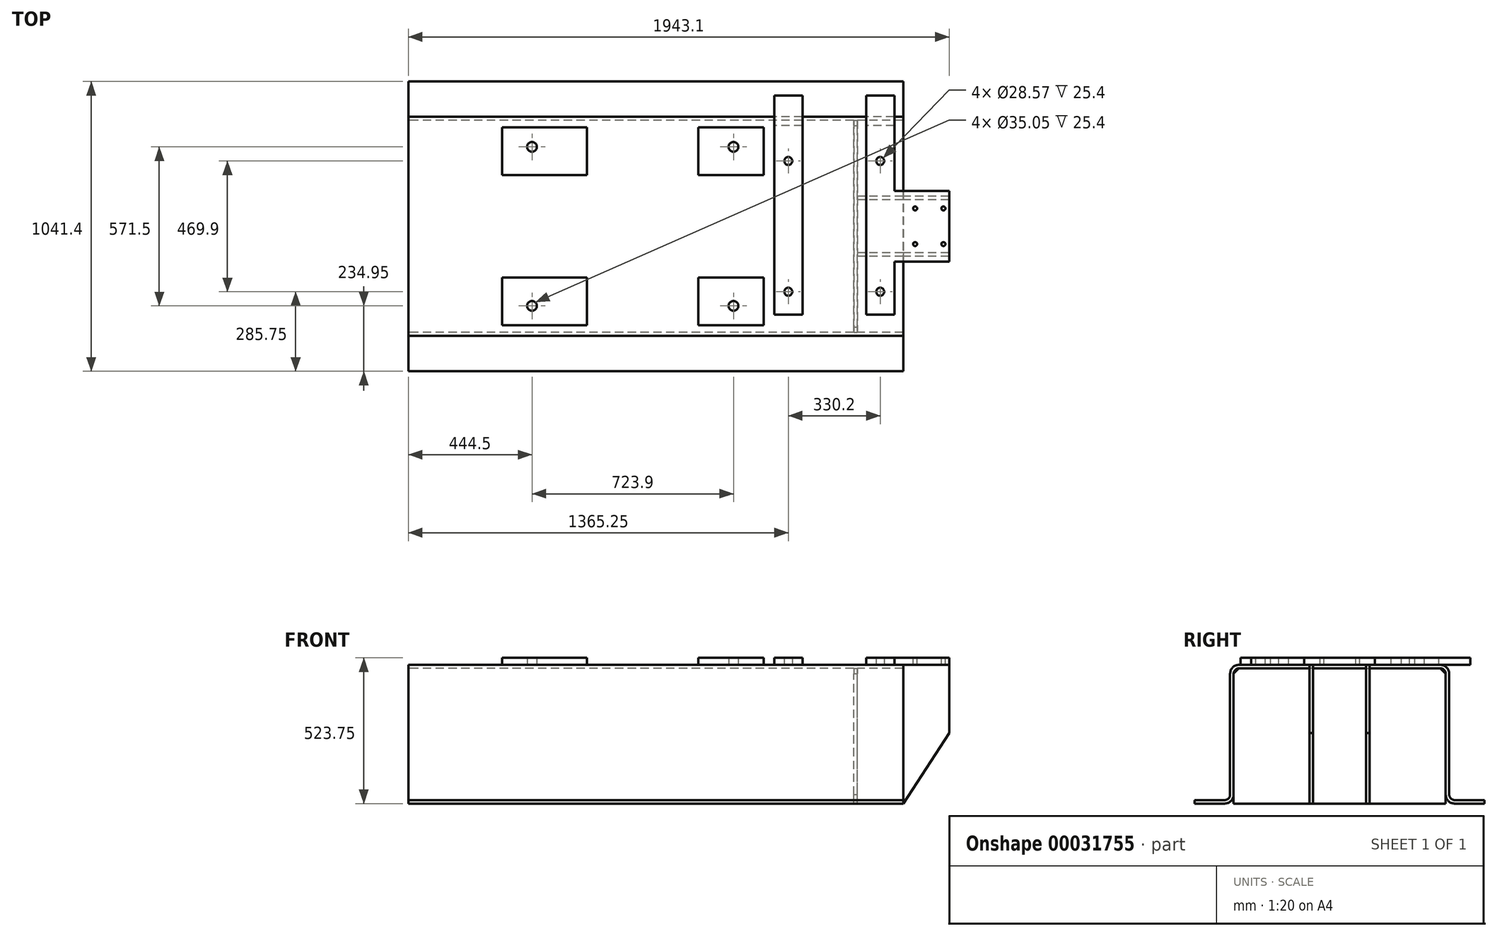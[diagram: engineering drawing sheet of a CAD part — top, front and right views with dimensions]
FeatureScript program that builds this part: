
annotation { "Feature Type Name" : "Feature", "Feature Type Description" : "" }
export const myFeature = defineFeature(function(context is Context, id is Id, definition is map)
    precondition{}
    {
        {
            var Q0;
            Q0=qCreatedBy(makeId("Right.planeOp"),FACE);
            var sketch = newSketch(context, id + "F0", { "sketchPlane" : qUnion([Q0])});
            skLineSegment(sketch, "E0", {"start": v(-520.7, 0) * mm, "end": v(-412.75, 0) * mm});
            skLineSegment(sketch, "E1.0", {"start": v(-520.7, 12.7) * mm, "end": v(-412.75, 12.7) * mm});
            skLineSegment(sketch, "E2", {"start": v(-520.7, 0) * mm, "end": v(-520.7, 12.7) * mm});
            skLineSegment(sketch, "E3", {"start": v(0, 498.35) * mm, "end": v(0, -237.5) * mm, "construction": true});
            skLineSegment(sketch, "E4.0", {"start": v(-381, 31.75) * mm, "end": v(-381, 466.6) * mm});
            skLineSegment(sketch, "E5.0", {"start": v(-393.7, 31.75) * mm, "end": v(-393.7, 466.6) * mm});
            skLineSegment(sketch, "E6.0", {"start": v(-361.95, 498.35) * mm, "end": v(0, 498.35) * mm});
            skLineSegment(sketch, "E7.0", {"start": v(-361.95, 485.65) * mm, "end": v(0, 485.65) * mm});
            skPoint(sketch, "E8.orphan", {"position": v(-520.7, 181.66) * mm});
            skPoint(sketch, "E9.visualSharp", {"position": v(-381, 485.65) * mm});
            skArc(sketch, "E9.filletArc", {"start": v(-361.95, 485.65) * mm, "mid": v(-375.42, 480.07) * mm, "end": v(-381, 466.6) * mm});
            skPoint(sketch, "E10.visualSharp", {"position": v(-393.7, 12.7) * mm});
            skArc(sketch, "E10.filletArc", {"start": v(-412.75, 12.7) * mm, "mid": v(-399.28, 18.28) * mm, "end": v(-393.7, 31.75) * mm});
            skPoint(sketch, "E11.visualSharp", {"position": v(-393.7, 498.35) * mm});
            skArc(sketch, "E11.filletArc", {"start": v(-361.95, 498.35) * mm, "mid": v(-384.4, 489.05) * mm, "end": v(-393.7, 466.6) * mm});
            skPoint(sketch, "E12.visualSharp", {"position": v(-381, 0) * mm});
            skArc(sketch, "E12.filletArc", {"start": v(-412.75, 0) * mm, "mid": v(-390.3, 9.3) * mm, "end": v(-381, 31.75) * mm});
            skLineSegment(sketch, "E13.MirrorCS", {"start": v(520.7, 0) * mm, "end": v(520.7, 12.7) * mm});
            skArc(sketch, "E14.MirrorCS", {"start": v(412.75, 12.7) * mm, "mid": v(399.28, 18.28) * mm, "end": v(393.7, 31.75) * mm});
            skArc(sketch, "E15.MirrorCS", {"start": v(412.75, 0) * mm, "mid": v(390.3, 9.3) * mm, "end": v(381, 31.75) * mm});
            skPoint(sketch, "E16.MirrorP", {"position": v(393.7, 12.7) * mm});
            skPoint(sketch, "E17.MirrorP", {"position": v(381, 0) * mm});
            skLineSegment(sketch, "E18.MirrorCS", {"start": v(520.7, 0) * mm, "end": v(412.75, 0) * mm});
            skLineSegment(sketch, "E19.MirrorCS", {"start": v(520.7, 12.7) * mm, "end": v(412.75, 12.7) * mm});
            skLineSegment(sketch, "E20.MirrorCS", {"start": v(393.7, 31.75) * mm, "end": v(393.7, 466.6) * mm});
            skLineSegment(sketch, "E21.MirrorCS", {"start": v(381, 31.75) * mm, "end": v(381, 466.6) * mm});
            skArc(sketch, "E22.MirrorCS", {"start": v(361.95, 485.65) * mm, "mid": v(375.42, 480.07) * mm, "end": v(381, 466.6) * mm});
            skArc(sketch, "E23.MirrorCS", {"start": v(361.95, 498.35) * mm, "mid": v(384.4, 489.05) * mm, "end": v(393.7, 466.6) * mm});
            skPoint(sketch, "E24.MirrorP", {"position": v(381, 485.65) * mm});
            skPoint(sketch, "E25.MirrorP", {"position": v(393.7, 498.35) * mm});
            skLineSegment(sketch, "E26.MirrorCS", {"start": v(361.95, 485.65) * mm, "end": v(0, 485.65) * mm});
            skLineSegment(sketch, "E27.MirrorCS", {"start": v(361.95, 498.35) * mm, "end": v(0, 498.35) * mm});
            skSolve(sketch);
        }
        {
            var Q0;
            Q0 = qSketchRegion(id + "F0", true);
            extrude(context, id + "F1", {"entities" : qUnion([Q0]), "endBound" : BoundingType.SYMMETRIC, "depth" : 1778 * mm});
        }
        {
            var Q0;
            Q0=makeQuery(id+"F1.opExtrude","SWEPT_FACE",FACE,{"disambiguationData":[OSD([sQuery(id+"F0.wireOp",EDGE,"E6.0"),sQuery(id+"F0.wireOp",EDGE,"E27.MirrorCS")])]});
            var sketch = newSketch(context, id + "F2", { "sketchPlane" : qUnion([Q0])});
            skLineSegment(sketch, "E28.0", {"start": v(641.35, 361.95) * mm, "end": v(641.35, -361.95) * mm, "construction": true});
            skLineSegment(sketch, "E29.0", {"start": v(-82.55, 361.95) * mm, "end": v(-82.55, -361.95) * mm, "construction": true});
            skLineSegment(sketch, "E30", {"start": v(-872.47, 0) * mm, "end": v(1054.1, 0) * mm, "construction": true});
            skLineSegment(sketch, "E31.0", {"start": v(476.25, 361.95) * mm, "end": v(476.25, -361.95) * mm, "construction": true});
            skLineSegment(sketch, "E32.0", {"start": v(806.45, 361.95) * mm, "end": v(806.45, -361.95) * mm, "construction": true});
            skLineSegment(sketch, "E33.0", {"start": v(425.45, 469.9) * mm, "end": v(425.45, -317.5) * mm});
            skLineSegment(sketch, "E34.0", {"start": v(527.05, 469.9) * mm, "end": v(527.05, -317.5) * mm});
            skLineSegment(sketch, "E35.0", {"start": v(755.65, 469.9) * mm, "end": v(755.65, -317.5) * mm});
            skLineSegment(sketch, "E36.0", {"start": v(1054.1, 127) * mm, "end": v(1054.1, -127) * mm});
            skLineSegment(sketch, "E37.0", {"start": v(425.45, 469.9) * mm, "end": v(527.05, 469.9) * mm});
            skLineSegment(sketch, "E38.0", {"start": v(755.65, -317.5) * mm, "end": v(857.25, -317.5) * mm});
            skLineSegment(sketch, "E39.trimOffspring", {"start": v(755.65, 469.9) * mm, "end": v(857.25, 469.9) * mm});
            skLineSegment(sketch, "E40.trimOffspring", {"start": v(527.05, -317.5) * mm, "end": v(425.45, -317.5) * mm});
            skLineSegment(sketch, "E41.0", {"start": v(857.25, 469.9) * mm, "end": v(857.25, 127) * mm});
            skLineSegment(sketch, "E42.trimOffspring", {"start": v(857.25, -127) * mm, "end": v(1054.1, -127) * mm});
            skLineSegment(sketch, "E43.trimOffspring", {"start": v(857.25, 127) * mm, "end": v(1054.1, 127) * mm});
            skLineSegment(sketch, "E44.trimOffspring", {"start": v(857.25, -127) * mm, "end": v(857.25, -317.5) * mm});
            skLineSegment(sketch, "E45.0", {"start": v(-872.47, 234.95) * mm, "end": v(1054.1, 234.95) * mm, "construction": true});
            skCircle(sketch, "E46", {"center": v(476.25, 234.95) * mm, "radius": 14.29 * mm});
            skCircle(sketch, "E47", {"center": v(806.45, 234.95) * mm, "radius": 14.29 * mm});
            skCircle(sketch, "E48.MirrorC", {"center": v(806.45, -234.95) * mm, "radius": 14.29 * mm});
            skCircle(sketch, "E49.MirrorC", {"center": v(476.25, -234.95) * mm, "radius": 14.29 * mm});
            skSolve(sketch);
        }
        {
            var Q0;
            Q0 = qSketchRegion(id + "F2", true);
            extrude(context, id + "F3", {"entities" : qUnion([Q0]), "operationType" : NewBodyOperationType.ADD, "depth" : 25.4 * mm});
        }
        {
            var Q0;
            Q0=makeQuery(id+"F3.opExtrude","CAP_FACE",FACE,{"disambiguationData":[OSD([sQuery(id+"F2.wireOp",EDGE,"E35.0"),sQuery(id+"F2.wireOp",EDGE,"E36.0"),sQuery(id+"F2.wireOp",EDGE,"E38.0"),sQuery(id+"F2.wireOp",EDGE,"E39.trimOffspring"),sQuery(id+"F2.wireOp",EDGE,"E41.0"),sQuery(id+"F2.wireOp",EDGE,"E42.trimOffspring"),sQuery(id+"F2.wireOp",EDGE,"E43.trimOffspring"),sQuery(id+"F2.wireOp",EDGE,"E44.trimOffspring"),sQuery(id+"F2.wireOp",EDGE,"E47"),sQuery(id+"F2.wireOp",EDGE,"E48.MirrorC")])],"isStart":false});
            var sketch = newSketch(context, id + "F4", { "sketchPlane" : qUnion([Q0])});
            skLineSegment(sketch, "E50", {"start": v(806.45, 234.95) * mm, "end": v(806.45, -249.24) * mm, "construction": true});
            skLineSegment(sketch, "E51", {"start": v(0, 0) * mm, "end": v(1216.03, 0) * mm, "construction": true});
            skPoint(sketch, "E51.endSnap0", {"position": v(1054.1, 0) * mm});
            skLineSegment(sketch, "E52.0", {"start": v(931.93, 234.95) * mm, "end": v(931.93, -249.24) * mm, "construction": true});
            skLineSegment(sketch, "E53.0", {"start": v(1033.53, 234.95) * mm, "end": v(1033.53, -249.24) * mm, "construction": true});
            skLineSegment(sketch, "E54.0", {"start": v(0, 64.52) * mm, "end": v(1216.03, 64.52) * mm, "construction": true});
            skLineSegment(sketch, "E55.0", {"start": v(0, -63.5) * mm, "end": v(1216.03, -63.5) * mm, "construction": true});
            skCircle(sketch, "E56", {"center": v(931.93, 64.52) * mm, "radius": 7.14 * mm});
            skCircle(sketch, "E57", {"center": v(1033.53, 64.52) * mm, "radius": 7.14 * mm});
            skCircle(sketch, "E58", {"center": v(1033.53, -63.5) * mm, "radius": 7.14 * mm});
            skCircle(sketch, "E59", {"center": v(931.93, -63.5) * mm, "radius": 7.14 * mm});
            skSolve(sketch);
        }
        {
            var Q0;
            Q0 = qSketchRegion(id + "F4", true);
            extrude(context, id + "F5", {"entities" : qUnion([Q0]), "operationType" : NewBodyOperationType.REMOVE, "endBound" : BoundingType.THROUGH_ALL, "oppositeDirection" : true, "depth" : 25.4 * mm});
        }
        {
            var Q0;
            Q0=makeQuery(id+"F1.opExtrude","CAP_FACE",FACE,{"disambiguationData":[OSD([sQuery(id+"F0.wireOp",EDGE,"E0"),sQuery(id+"F0.wireOp",EDGE,"E1.0"),sQuery(id+"F0.wireOp",EDGE,"E2"),sQuery(id+"F0.wireOp",EDGE,"E4.0"),sQuery(id+"F0.wireOp",EDGE,"E5.0"),sQuery(id+"F0.wireOp",EDGE,"E6.0"),sQuery(id+"F0.wireOp",EDGE,"E7.0"),sQuery(id+"F0.wireOp",EDGE,"E9.filletArc"),sQuery(id+"F0.wireOp",EDGE,"E10.filletArc"),sQuery(id+"F0.wireOp",EDGE,"E11.filletArc"),sQuery(id+"F0.wireOp",EDGE,"E12.filletArc"),sQuery(id+"F0.wireOp",EDGE,"E13.MirrorCS"),sQuery(id+"F0.wireOp",EDGE,"E14.MirrorCS"),sQuery(id+"F0.wireOp",EDGE,"E15.MirrorCS"),sQuery(id+"F0.wireOp",EDGE,"E18.MirrorCS"),sQuery(id+"F0.wireOp",EDGE,"E19.MirrorCS"),sQuery(id+"F0.wireOp",EDGE,"E22.MirrorCS"),sQuery(id+"F0.wireOp",EDGE,"E23.MirrorCS"),sQuery(id+"F0.wireOp",EDGE,"E26.MirrorCS"),sQuery(id+"F0.wireOp",EDGE,"E27.MirrorCS"),sQuery(id+"F0.wireOp",EDGE,"E20.MirrorCS"),sQuery(id+"F0.wireOp",EDGE,"E21.MirrorCS")])],"isStart":false});
            cPlane(context, id + "F6", {"entities" : qUnion([Q0]), "cplaneType" : CPlaneType.OFFSET, "offset" : 165.1 * mm, "oppositeDirection" : true, "width" : 152.4 * mm, "height" : 152.4 * mm});
        }
        {
            var Q0;
            Q0=qCreatedBy(id+"F6.planeOp",FACE);
            var sketch = newSketch(context, id + "F7", { "sketchPlane" : qUnion([Q0])});
            skLineSegment(sketch, "E60.0", {"start": v(-361.95, 485.65) * mm, "end": v(361.95, 485.65) * mm});
            skLineSegment(sketch, "E61.0", {"start": v(-381, 0) * mm, "end": v(-381, 466.6) * mm});
            skLineSegment(sketch, "E62.0", {"start": v(381, 0) * mm, "end": v(381, 466.6) * mm});
            skLineSegment(sketch, "E63.0", {"start": v(381, 0) * mm, "end": v(-381, 0) * mm});
            skPoint(sketch, "E64.orphan", {"position": v(412.75, 0) * mm});
            skPoint(sketch, "E65.orphan", {"position": v(520.7, 0) * mm});
            skPoint(sketch, "E66.orphan", {"position": v(381, 31.75) * mm});
            skPoint(sketch, "E67.orphan", {"position": v(-381, 31.75) * mm});
            skLineSegment(sketch, "E68", {"start": v(-381, 466.6) * mm, "end": v(-361.95, 485.65) * mm});
            skLineSegment(sketch, "E69", {"start": v(361.95, 485.65) * mm, "end": v(381, 466.6) * mm});
            skSolve(sketch);
        }
        {
            var Q0;
            Q0 = qSketchRegion(id + "F7", true);
            extrude(context, id + "F8", {"entities" : qUnion([Q0]), "operationType" : NewBodyOperationType.ADD, "oppositeDirection" : true, "depth" : 12.7 * mm});
        }
        {
            var Q0;
            Q0=makeQuery(id+"F8.opExtrude","CAP_FACE",FACE,{"disambiguationData":[OSD([sQuery(id+"F7.wireOp",EDGE,"E60.0"),sQuery(id+"F7.wireOp",EDGE,"E61.0"),sQuery(id+"F7.wireOp",EDGE,"E62.0"),sQuery(id+"F7.wireOp",EDGE,"E63.0"),sQuery(id+"F7.wireOp",EDGE,"E68"),sQuery(id+"F7.wireOp",EDGE,"E69")])],"isStart":true});
            var sketch = newSketch(context, id + "F9", { "sketchPlane" : qUnion([Q0])});
            skLineSegment(sketch, "E70", {"start": v(0, 0) * mm, "end": v(0, 673.02) * mm, "construction": true});
            skPoint(sketch, "E70.endSnap0", {"position": v(0, 0) * mm});
            skLineSegment(sketch, "E71.0", {"start": v(-95.25, 0) * mm, "end": v(-95.25, 673.02) * mm, "construction": true});
            skLineSegment(sketch, "E72.bottom", {"start": v(-95.25, 0) * mm, "end": v(-107.95, 0) * mm});
            skLineSegment(sketch, "E72.top", {"start": v(-95.25, 485.65) * mm, "end": v(-107.95, 485.65) * mm});
            skLineSegment(sketch, "E72.left", {"start": v(-95.25, 0) * mm, "end": v(-95.25, 485.65) * mm});
            skLineSegment(sketch, "E72.right", {"start": v(-107.95, 0) * mm, "end": v(-107.95, 485.65) * mm});
            skSolve(sketch);
        }
        {
            var Q0;
            Q0 = qSketchRegion(id + "F9", true);
            var Q1;
            Q1=makeQuery(id+"F3.opExtrude","SWEPT_FACE",FACE,{"disambiguationData":[OSD([sQuery(id+"F2.wireOp",EDGE,"E36.0")])]});
            extrude(context, id + "F10", {"entities" : qUnion([Q0]), "endBound" : BoundingType.UP_TO_SURFACE, "endBoundEntityFace" : qUnion([Q1]), "depth" : 25.4 * mm});
        }
        {
            var Q0;
            Q0=makeQuery(id+"F10.opExtrude","SWEPT_FACE",FACE,{"disambiguationData":[OSD([sQuery(id+"F9.wireOp",EDGE,"E72.right")])]});
            var sketch = newSketch(context, id + "F11", { "sketchPlane" : qUnion([Q0])});
            skPoint(sketch, "E73.oppositeSnap0", {"position": v(889, 485.65) * mm});
            skLineSegment(sketch, "E73.bottom", {"start": v(1054.1, 485.65) * mm, "end": v(889, 485.65) * mm});
            skLineSegment(sketch, "E73.top", {"start": v(1054.1, 498.55) * mm, "end": v(889, 498.55) * mm});
            skLineSegment(sketch, "E73.left", {"start": v(1054.1, 485.65) * mm, "end": v(1054.1, 498.55) * mm});
            skLineSegment(sketch, "E73.right", {"start": v(889, 485.65) * mm, "end": v(889, 498.55) * mm});
            skSolve(sketch);
        }
        {
            var Q0;
            Q0 = qSketchRegion(id + "F11", true);
            extrude(context, id + "F12", {"entities" : qUnion([Q0]), "oppositeDirection" : true, "depth" : 12.7 * mm});
        }
        {
            var Q0;
            Q0=makeQuery(id+"F12.opExtrude","SWEPT_BODY",BODY,{"disambiguationData":[OSD([sQuery(id+"F11.wireOp",EDGE,"E73.bottom"),sQuery(id+"F11.wireOp",EDGE,"E73.top"),sQuery(id+"F11.wireOp",EDGE,"E73.left"),sQuery(id+"F11.wireOp",EDGE,"E73.right")])]});
            var Q1;
            Q1=makeQuery(id+"F10.opExtrude","SWEPT_BODY",BODY,{"disambiguationData":[OSD([sQuery(id+"F9.wireOp",EDGE,"E72.bottom"),sQuery(id+"F9.wireOp",EDGE,"E72.top"),sQuery(id+"F9.wireOp",EDGE,"E72.left"),sQuery(id+"F9.wireOp",EDGE,"E72.right")])]});
            booleanBodies(context, id + "F13", {"operationType" : BooleanOperationType.UNION, "tools" : qUnion([Q0, Q1])});
        }
        {
            var Q0;
            Q0=makeQuery(id+"F13.opBoolean","MERGE",FACE,{"derivedFrom":[makeQuery(id+"F10.opExtrude","SWEPT_FACE",FACE,{"disambiguationData":[OSD([sQuery(id+"F9.wireOp",EDGE,"E72.right")])]}),makeQuery(id+"F12.opExtrude","CAP_FACE",FACE,{"disambiguationData":[OSD([sQuery(id+"F11.wireOp",EDGE,"E73.bottom"),sQuery(id+"F11.wireOp",EDGE,"E73.top"),sQuery(id+"F11.wireOp",EDGE,"E73.left"),sQuery(id+"F11.wireOp",EDGE,"E73.right")])],"isStart":true})]});
            var sketch = newSketch(context, id + "F14", { "sketchPlane" : qUnion([Q0])});
            skLineSegment(sketch, "E74.0", {"start": v(1054.1, 0) * mm, "end": v(723.9, 0) * mm, "construction": true});
            skLineSegment(sketch, "E75.0", {"start": v(889, 0) * mm, "end": v(889, 12.7) * mm, "construction": true});
            skLineSegment(sketch, "E76.0", {"start": v(1054.1, 254) * mm, "end": v(723.9, 254) * mm, "construction": true});
            skLineSegment(sketch, "E77", {"start": v(1054.1, 254) * mm, "end": v(889, 0) * mm});
            skLineSegment(sketch, "E78", {"start": v(889, 0) * mm, "end": v(1054.1, 0) * mm});
            skLineSegment(sketch, "E79", {"start": v(1054.1, 0) * mm, "end": v(1054.1, 254) * mm});
            skSolve(sketch);
        }
        {
            var Q0;
            Q0 = qSketchRegion(id + "F14", true);
            extrude(context, id + "F15", {"entities" : qUnion([Q0]), "operationType" : NewBodyOperationType.REMOVE, "endBound" : BoundingType.THROUGH_ALL, "oppositeDirection" : true, "depth" : 25.4 * mm});
        }
        {
            var Q0;
            Q0=makeQuery(id+"F12.opExtrude","SWEPT_BODY",BODY,{"disambiguationData":[OSD([sQuery(id+"F11.wireOp",EDGE,"E73.bottom"),sQuery(id+"F11.wireOp",EDGE,"E73.top"),sQuery(id+"F11.wireOp",EDGE,"E73.left"),sQuery(id+"F11.wireOp",EDGE,"E73.right")])]});
            var Q1;
            Q1=qCreatedBy(makeId("Front.planeOp"),FACE);
            mirror(context, id + "F16", {"entities" : qUnion([Q0]), "mirrorPlane" : qUnion([Q1])});
        }
        {
            var Q0;
            {var subQ0=sQuery(id+"F0.wireOp",EDGE,"E6.0");var subQ1=sQuery(id+"F0.wireOp",EDGE,"E27.MirrorCS");var subQ9=sQuery(id+"F0.wireOp",EDGE,"E11.filletArc");Q0=makeQuery(id+"F3.boolean.opBoolean","SPLIT",FACE,{"disambiguationData":[TD([makeQuery(id+"F1.opExtrude","SWEPT_FACE",FACE,{"disambiguationData":[OSD([subQ9])]})])],"derivedFrom":makeQuery(id+"F1.opExtrude","SWEPT_FACE",FACE,{"disambiguationData":[OSD([subQ0,subQ1])]})});}
            var sketch = newSketch(context, id + "F17", { "sketchPlane" : qUnion([Q0])});
            skLineSegment(sketch, "E80", {"start": v(-968.8, 0) * mm, "end": v(1260.8, 0) * mm, "construction": true});
            skPoint(sketch, "E80.endSnap0", {"position": v(-889, 0) * mm});
            skCircle(sketch, "E81.0", {"center": v(476.25, 234.95) * mm, "radius": 14.29 * mm, "construction": true});
            skCircle(sketch, "E82.0", {"center": v(806.45, 234.95) * mm, "radius": 14.29 * mm, "construction": true});
            skLineSegment(sketch, "E83", {"start": v(476.25, 234.95) * mm, "end": v(806.45, 234.95) * mm, "construction": true});
            skLineSegment(sketch, "E84", {"start": v(641.35, 234.95) * mm, "end": v(641.35, -183.34) * mm, "construction": true});
            skLineSegment(sketch, "E85.0", {"start": v(-82.55, 234.95) * mm, "end": v(-82.55, -183.34) * mm, "construction": true});
            skLineSegment(sketch, "E86.0", {"start": v(-968.8, 184.15) * mm, "end": v(1260.8, 184.15) * mm, "construction": true});
            skLineSegment(sketch, "E87.0", {"start": v(-968.8, 355.6) * mm, "end": v(1260.8, 355.6) * mm, "construction": true});
            skLineSegment(sketch, "E88.0", {"start": v(-247.65, 234.95) * mm, "end": v(-247.65, -183.34) * mm, "construction": true});
            skLineSegment(sketch, "E89.0", {"start": v(-552.45, 355.6) * mm, "end": v(-552.45, -183.34) * mm, "construction": true});
            skLineSegment(sketch, "E90.0", {"start": v(152.4, 234.95) * mm, "end": v(152.4, -183.34) * mm, "construction": true});
            skLineSegment(sketch, "E91.0", {"start": v(387.35, 355.6) * mm, "end": v(387.35, -183.34) * mm, "construction": true});
            skLineSegment(sketch, "E92.bottom", {"start": v(-552.45, 355.6) * mm, "end": v(-247.65, 355.6) * mm});
            skLineSegment(sketch, "E92.top", {"start": v(-552.45, 184.15) * mm, "end": v(-247.65, 184.15) * mm});
            skLineSegment(sketch, "E92.left", {"start": v(-552.45, 355.6) * mm, "end": v(-552.45, 184.15) * mm});
            skLineSegment(sketch, "E92.right", {"start": v(-247.65, 355.6) * mm, "end": v(-247.65, 184.15) * mm});
            skLineSegment(sketch, "E93.bottom", {"start": v(387.35, 355.6) * mm, "end": v(152.4, 355.6) * mm});
            skLineSegment(sketch, "E93.top", {"start": v(387.35, 184.15) * mm, "end": v(152.4, 184.15) * mm});
            skLineSegment(sketch, "E93.left", {"start": v(387.35, 355.6) * mm, "end": v(387.35, 184.15) * mm});
            skLineSegment(sketch, "E93.right", {"start": v(152.4, 355.6) * mm, "end": v(152.4, 184.15) * mm});
            skLineSegment(sketch, "E94.0", {"start": v(-968.8, 285.75) * mm, "end": v(1260.8, 285.75) * mm, "construction": true});
            skLineSegment(sketch, "E95.0", {"start": v(-444.5, 285.75) * mm, "end": v(-444.5, -183.34) * mm, "construction": true});
            skLineSegment(sketch, "E96.MirrorCS", {"start": v(279.4, 285.75) * mm, "end": v(279.4, -183.34) * mm, "construction": true});
            skCircle(sketch, "E97", {"center": v(-444.5, 285.75) * mm, "radius": 17.53 * mm});
            skCircle(sketch, "E98", {"center": v(279.4, 285.75) * mm, "radius": 17.53 * mm});
            skCircle(sketch, "E99.MirrorC", {"center": v(279.4, -285.75) * mm, "radius": 17.53 * mm});
            skLineSegment(sketch, "E100.MirrorCS", {"start": v(387.35, -355.6) * mm, "end": v(387.35, -184.15) * mm});
            skLineSegment(sketch, "E101.MirrorCS", {"start": v(-552.45, -355.6) * mm, "end": v(-247.65, -355.6) * mm});
            skLineSegment(sketch, "E102.MirrorCS", {"start": v(387.35, -184.15) * mm, "end": v(152.4, -184.15) * mm});
            skLineSegment(sketch, "E103.MirrorCS", {"start": v(387.35, -355.6) * mm, "end": v(152.4, -355.6) * mm});
            skLineSegment(sketch, "E104.MirrorCS", {"start": v(-247.65, -355.6) * mm, "end": v(-247.65, -184.15) * mm});
            skLineSegment(sketch, "E105.MirrorCS", {"start": v(-552.45, -355.6) * mm, "end": v(-552.45, -184.15) * mm});
            skLineSegment(sketch, "E106.MirrorCS", {"start": v(152.4, -355.6) * mm, "end": v(152.4, -184.15) * mm});
            skLineSegment(sketch, "E107.MirrorCS", {"start": v(-552.45, -184.15) * mm, "end": v(-247.65, -184.15) * mm});
            skCircle(sketch, "E108.MirrorC", {"center": v(-444.5, -285.75) * mm, "radius": 17.53 * mm});
            skSolve(sketch);
        }
        {
            var Q0;
            Q0 = qSketchRegion(id + "F17", true);
            extrude(context, id + "F18", {"entities" : qUnion([Q0]), "operationType" : NewBodyOperationType.ADD, "depth" : 25.4 * mm});
        }
    });
